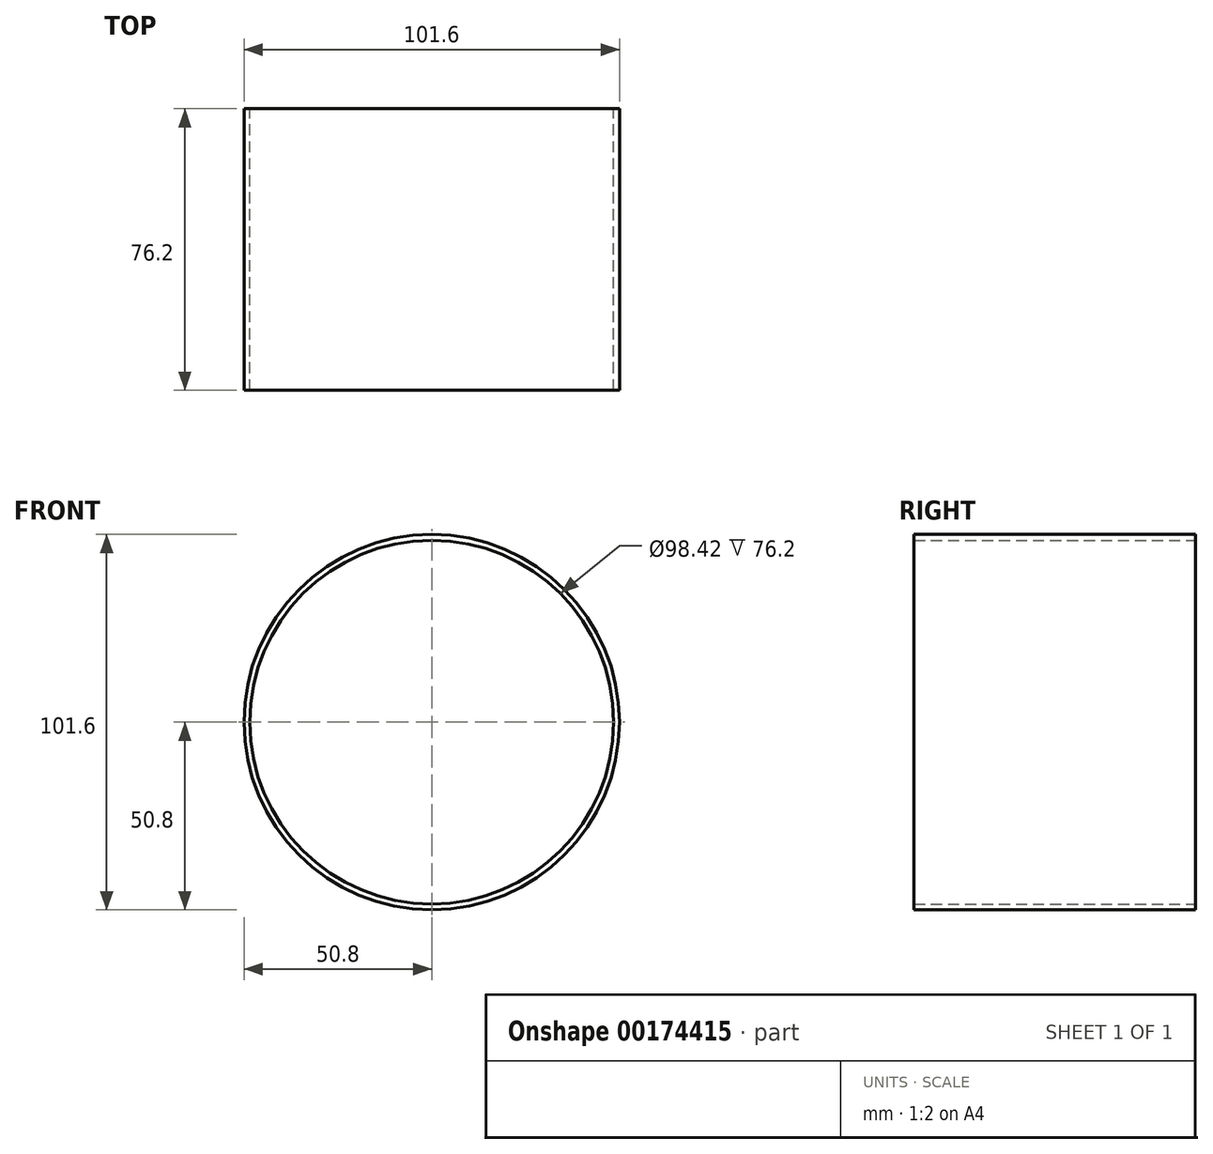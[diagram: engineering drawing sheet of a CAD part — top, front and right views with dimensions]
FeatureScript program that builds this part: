
annotation { "Feature Type Name" : "Feature", "Feature Type Description" : "" }
export const myFeature = defineFeature(function(context is Context, id is Id, definition is map)
    precondition{}
    {
        {
            var Q0;
            Q0=qCreatedBy(makeId("Front.planeOp"),FACE);
            var sketch = newSketch(context, id + "F0", { "sketchPlane" : qUnion([Q0])});
            skCircle(sketch, "E0", {"center": v(0, 0) * mm, "radius": 50.8 * mm});
            skCircle(sketch, "E1.0", {"center": v(0, 0) * mm, "radius": 49.21 * mm});
            skSolve(sketch);
        }
        {
            var Q0;
            Q0 = qSketchRegion(id + "F0", true);
            extrude(context, id + "F1", {"entities" : qUnion([Q0]), "depth" : 76.2 * mm, "offsetDistance" : 25.4 * mm});
        }
    });
